# Revit family: IS_Extra_A7624_BIM_GB
name_source: partatom
category: Plumbing Fixtures
units: mm (PartAtom-declared; Revit-internal decimal feet)

## family parameters
Always vertical = No
Cut with Voids When Loaded = No
OmniClass Number = 23.45.55.17
OmniClass Title = Mixing Faucets
Part Type = Normal
Room Calculation Point = No
Round Connector Dimension = Use Diameter
Shared = No
Work Plane-Based = No

## types (4) — shared parameters
Accessories = https://www.idealstandard.co.uk
AreaUnits = millimetres
BIMObjectName = Showermanualwatersupplysets_Extra_A7624_IdealStandard
BIMobject category = Taps & Mixers
BIMobject category code = sanitary-taps-mixers
BIMobject main category = Sanitary
BIMobject main category code = sanitary
Brand = Ideal standard
Brand url = http://www.idealstandard.co.uk
Category = Sanitary
Classification = Taps & Mixers
ConnectionType = plumbing
CurrencyUnit = £
CurrentRevision = 1
Date of publishing = 09/11/2022
Description = Extra Shower mixer built-in kit 2/ a1000nu a2
DurationUnit = years
Edition number = 1
ElementType = Fixed
ExpectedLife = 5
FaucetFunction = Single lever shower Mixer
FaucetOperation = Single lever shower Mixer
FaucetTopDescription = Single lever shower Mixer
FaucetType = Single lever shower Mixer
Features = Extra Shower mixer built-in kit 2/ a1000nu a2
Help = https://www.idealstandard.co.uk
IFC Classification = Sanitary Terminal
IfcExportAs = IfcValveType
IfcExportType = FAUCET
Installation instructions = https://www.idealstandard.co.uk
InstallationInstructions = https://www.idealstandard.co.uk
LinearUnits = millimetres
MaintenanceInformation = https://www.idealstandard.co.uk
Manufacturer = Ideal Standard
Manufacturer name = Ideal Standard
ManufacturerURL = https://www.idealstandard.co.uk
Masterformat 2014 Code = 22 40 00
Masterformat 2014 Description = Plumbing Fixtures
Material = Brass
Material main = Brass
NBS Reference Code = 45-35-70/335
NBS Reference Description = Shower mixers
Name = IS_IdealStandard_Showermanualwatersupplysets_Extra_A7624
NettWeight = 1.342
NominalDepth = 70 mm
NominalHeight = 187 mm
NominalLength = 70 mm
NominalWidth = 163 mm
OmniClass Code = 23-31 11 00
OmniClass Description = Faucets
PredefinedType = Fixed
Product Guid = 95431ec4-a0e9-47b6-a4fe-205dc94ec5f6
Product SKU = A7624
Product certification = https://www.idealstandard.co.uk
Product data url = https://bimobject.com
Product family = Extra
Product group = Taps & Mixers
Product name = Extra Shower mixer built-in kit 2/ a1000nu a2
Product url = https://www.idealstandard.co.uk
ProductInformation = https://www.idealstandard.co.uk
QR code = http://bimobject.com
Shape = cylindrical
Size = 163 x 71 x 187 mm
Space = Internal
SpareParts = https://www.idealstandard.co.uk
UNSPSC Code = 301815
URL = https://www.idealstandard.co.uk
Uniclass 1.4 Code = Mixer taps
Uniclass 1.4 Description = L725111
Uniclass 2.0 Code = Ac_20_64_30
Uniclass 2.0 Description = Fitting
Uniclass2015Code = Pr_40_20_87_78
Uniclass2015Title = Shower manual water supply sets
Uniclass2015Version = v1.27
Uniformat II Code = Plumbing Fixtures
Uniformat II Description = D2010
ValveMechanism = Single lever shower Mixer
ValveOperation = Single lever shower Mixer
Version = 1
VolumeUnits = Liters
WRASURL = https://www.wrasapprovals.co.uk
WarrantyDescription = manufacturer warranty
WarrantyDurationUnit = years
Weight Net (Kg) = 1.342
Youtube clip = https://www.youtube.com

## per-type parameters (varying)
| type | BarCode | Color | Finish | GTIN code | MainColor | Model | ModelNumber | ModelReference |
| A7624A2- Shower mixer built-in kit 2/ a1000nu a2 - Brushed Gold | 4015413353090 | Brush Gold | Brush Gold | https://4015413353090 | Brush Gold | A7624A2 | A7624A2 | hower mixer built-in kit 2/ a1000nu a2 - Brushed Gold |
| A7624A5 - Shower mixer built-in kit 2/ a1000nu a2 - Magnetic Grey | 4015413353120 | Magnetic Grey | Magnetic Grey | https://4015413353120 | Magnetic Grey | A7624A5 | A7624A5 | Shower mixer built-in kit 2/ a1000nu a2 - Magnetic Grey |
| A7624AA - Shower mixer built-in kit 2/ a1000nu a2 - Chrome | 4015413353069 | Chrome | Chrome | https://4015413353069 | Chrome | A7624AA | A7624AA | Shower mixer built-in kit 2/ a1000nu a2 - Chrome |
| A7624GN - Shower mixer built-in kit 2/ a1000nu a2 - Stainless Steel | 4015413353151 | Silver Storm | Silver Storm | https://4015413353151 | Silver Storm | A7624GN | A7624GN | Shower mixer built-in kit 2/ a1000nu a2 - Stainless Steel |

## geometry (parser evidence)
native form markers: Sweep x3
no freeform markers — native parametric forms only
